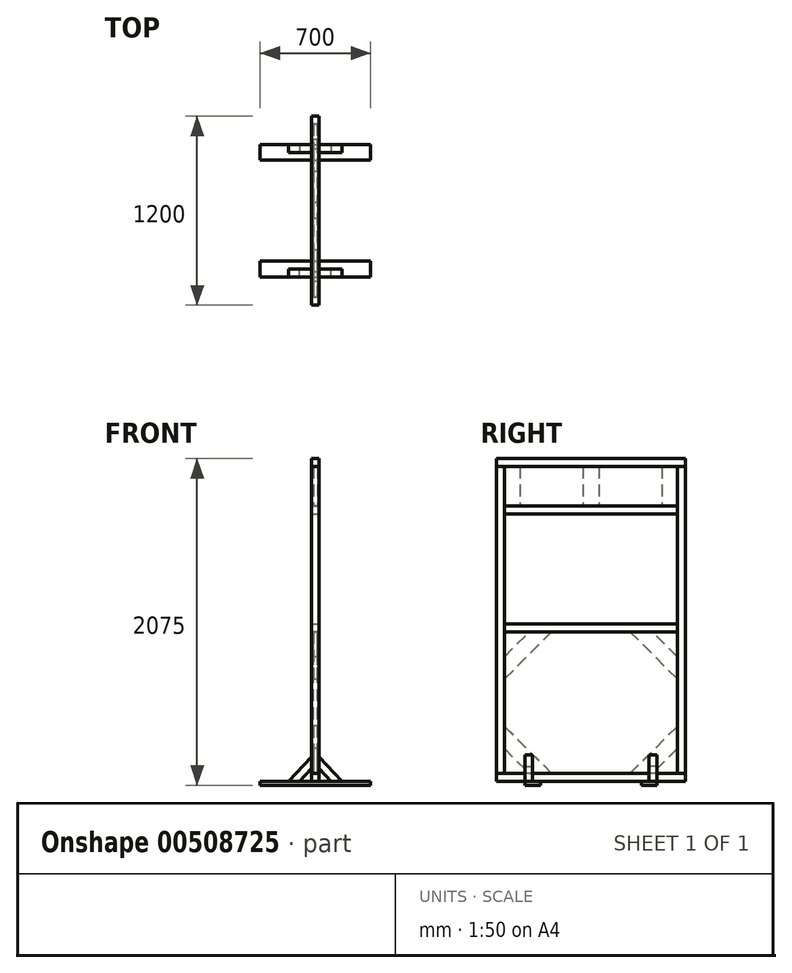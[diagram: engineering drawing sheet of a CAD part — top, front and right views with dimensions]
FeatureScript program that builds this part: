
annotation { "Feature Type Name" : "Feature", "Feature Type Description" : "" }
export const myFeature = defineFeature(function(context is Context, id is Id, definition is map)
    precondition{}
    {
        {
            var Q0;
            Q0=qCreatedBy(makeId("Top.planeOp"),FACE);
            var sketch = newSketch(context, id + "F0", { "sketchPlane" : qUnion([Q0])});
            skLineSegment(sketch, "E0.bottom", {"start": v(-350, 420) * mm, "end": v(350, 420) * mm});
            skLineSegment(sketch, "E0.top", {"start": v(-350, 320) * mm, "end": v(350, 320) * mm});
            skLineSegment(sketch, "E0.left", {"start": v(-350, 420) * mm, "end": v(-350, 320) * mm});
            skLineSegment(sketch, "E0.right", {"start": v(350, 420) * mm, "end": v(350, 320) * mm});
            skLineSegment(sketch, "E1.bottom", {"start": v(-350, -320) * mm, "end": v(350, -320) * mm});
            skLineSegment(sketch, "E1.top", {"start": v(-350, -420) * mm, "end": v(350, -420) * mm});
            skLineSegment(sketch, "E1.left", {"start": v(-350, -320) * mm, "end": v(-350, -420) * mm});
            skLineSegment(sketch, "E1.right", {"start": v(350, -320) * mm, "end": v(350, -420) * mm});
            skSolve(sketch);
        }
        {
            var Q0;
            Q0=makeQuery(id+"F0.imprint","IMPRINT",FACE,{"disambiguationData":[TD([[makeQuery(id+"F0.imprint","IMPRINT",EDGE,{"derivedFrom":sQuery(id+"F0.wireOp",EDGE,"E0.bottom")}),-1.0]])]});
            var Q1;
            Q1=makeQuery(id+"F0.imprint","IMPRINT",FACE,{"disambiguationData":[TD([[makeQuery(id+"F0.imprint","IMPRINT",EDGE,{"derivedFrom":sQuery(id+"F0.wireOp",EDGE,"E1.bottom")}),-1.0]])]});
            extrude(context, id + "F1", {"entities" : qUnion([Q0, Q1]), "depth" : 25 * mm});
        }
        {
            var Q0;
            Q0=makeQuery(id+"F1.opExtrude","CAP_FACE",FACE,{"disambiguationData":[OSD([sQuery(id+"F0.wireOp",EDGE,"E0.bottom"),sQuery(id+"F0.wireOp",EDGE,"E0.top"),sQuery(id+"F0.wireOp",EDGE,"E0.left"),sQuery(id+"F0.wireOp",EDGE,"E0.right")])],"isStart":false});
            var sketch = newSketch(context, id + "F2", { "sketchPlane" : qUnion([Q0])});
            skSolve(sketch);
        }
        {
            var Q0;
            Q0=makeQuery(id+"F1.opExtrude","CAP_FACE",FACE,{"disambiguationData":[OSD([sQuery(id+"F0.wireOp",EDGE,"E1.bottom"),sQuery(id+"F0.wireOp",EDGE,"E1.top"),sQuery(id+"F0.wireOp",EDGE,"E1.left"),sQuery(id+"F0.wireOp",EDGE,"E1.right")])],"isStart":false});
            var sketch = newSketch(context, id + "F3", { "sketchPlane" : qUnion([Q0])});
            skLineSegment(sketch, "E2.bottom", {"start": v(-25, 600) * mm, "end": v(25, 600) * mm});
            skLineSegment(sketch, "E2.top", {"start": v(-25, -600) * mm, "end": v(25, -600) * mm});
            skLineSegment(sketch, "E2.left", {"start": v(-25, 600) * mm, "end": v(-25, -600) * mm});
            skLineSegment(sketch, "E2.right", {"start": v(25, 600) * mm, "end": v(25, -600) * mm});
            skPoint(sketch, "E2.middle", {"position": v(0, 0) * mm});
            skSolve(sketch);
        }
        {
            var Q0;
            {var subQ0=sQuery(id+"F3.wireOp",EDGE,"E2.top");Q0=makeQuery(id+"F3.imprint","IMPRINT",FACE,{"disambiguationData":[TD([[makeQuery(id+"F3.imprint","IMPRINT",EDGE,{"derivedFrom":subQ0}),1.0]])]});}
            var Q1;
            {var subQ0=sQuery(id+"F3.wireOp",EDGE,"E2.left");var subQ1=makeQuery(id+"F1.opExtrude","CAP_EDGE",EDGE,{"disambiguationData":[OSD([sQuery(id+"F0.wireOp",EDGE,"E1.bottom")])],"isStart":false});var subQ2=makeQuery(id+"F3.imprint","INTERSECT",VERTEX,{"derivedFrom":[subQ1,subQ0]});Q1=makeQuery(id+"F3.imprint","IMPRINT",FACE,{"disambiguationData":[TD([[makeQuery(id+"F3.imprint","IMPRINT",EDGE,{"disambiguationData":[TD([[subQ2,-1.0]])],"derivedFrom":subQ0}),1.0]])]});}
            var Q2;
            {var subQ0=sQuery(id+"F3.wireOp",EDGE,"E2.bottom");Q2=makeQuery(id+"F3.imprint","IMPRINT",FACE,{"disambiguationData":[TD([[makeQuery(id+"F3.imprint","IMPRINT",EDGE,{"derivedFrom":subQ0}),-1.0]])]});}
            extrude(context, id + "F4", {"entities" : qUnion([Q0, Q1, Q2]), "depth" : 50 * mm});
        }
        {
            var Q0;
            Q0=makeQuery(id+"F2.imprint","IMPRINT",FACE,{"disambiguationData":[TD([[makeQuery(id+"F2.imprint","IMPRINT",EDGE,{"derivedFrom":makeQuery(id+"F1.opExtrude","CAP_EDGE",EDGE,{"disambiguationData":[OSD([sQuery(id+"F0.wireOp",EDGE,"E0.bottom")])],"isStart":false})}),-1.0]])]});
            var sketch = newSketch(context, id + "F5", { "sketchPlane" : qUnion([Q0])});
            skLineSegment(sketch, "E3.bottom", {"start": v(25, -600) * mm, "end": v(-25, -600) * mm});
            skLineSegment(sketch, "E3.top", {"start": v(25, 600) * mm, "end": v(-25, 600) * mm});
            skLineSegment(sketch, "E3.left", {"start": v(25, -600) * mm, "end": v(25, 600) * mm});
            skLineSegment(sketch, "E3.right", {"start": v(-25, -600) * mm, "end": v(-25, 600) * mm});
            skPoint(sketch, "E3.middle", {"position": v(0, 0) * mm});
            skSolve(sketch);
        }
        {
            var Q0;
            Q0=makeQuery(id+"F4.opExtrude","CAP_FACE",FACE,{"disambiguationData":[OSD([sQuery(id+"F3.wireOp",EDGE,"E2.bottom"),sQuery(id+"F3.wireOp",EDGE,"E2.top"),sQuery(id+"F3.wireOp",EDGE,"E2.left"),sQuery(id+"F3.wireOp",EDGE,"E2.right")])],"isStart":false});
            var sketch = newSketch(context, id + "F6", { "sketchPlane" : qUnion([Q0])});
            skSolve(sketch);
        }
        {
            var Q0;
            Q0=makeQuery(id+"F6.imprint","IMPRINT",FACE,{"disambiguationData":[TD([[makeQuery(id+"F6.imprint","IMPRINT",EDGE,{"derivedFrom":makeQuery(id+"F4.opExtrude","CAP_EDGE",EDGE,{"disambiguationData":[OSD([sQuery(id+"F3.wireOp",EDGE,"E2.bottom")])],"isStart":false})}),-1.0]])]});
            var sketch = newSketch(context, id + "F7", { "sketchPlane" : qUnion([Q0])});
            skLineSegment(sketch, "E4.bottom", {"start": v(25, -600) * mm, "end": v(-25, -600) * mm});
            skLineSegment(sketch, "E4.top", {"start": v(25, -550) * mm, "end": v(-25, -550) * mm});
            skLineSegment(sketch, "E4.left", {"start": v(25, -600) * mm, "end": v(25, -550) * mm});
            skLineSegment(sketch, "E4.right", {"start": v(-25, -600) * mm, "end": v(-25, -550) * mm});
            skPoint(sketch, "E4.middle", {"position": v(0, -575) * mm});
            skLineSegment(sketch, "E5.MirrorCS", {"start": v(25, 550) * mm, "end": v(-25, 550) * mm});
            skLineSegment(sketch, "E6.MirrorCS", {"start": v(25, 600) * mm, "end": v(25, 550) * mm});
            skLineSegment(sketch, "E7.MirrorCS", {"start": v(25, 600) * mm, "end": v(-25, 600) * mm});
            skLineSegment(sketch, "E8.MirrorCS", {"start": v(-25, 600) * mm, "end": v(-25, 550) * mm});
            skSolve(sketch);
        }
        {
            var Q0;
            Q0 = qSketchRegion(id + "F7", true);
            extrude(context, id + "F8", {"entities" : qUnion([Q0]), "depth" : 1950 * mm});
        }
        {
            var Q0;
            Q0=makeQuery(id+"F8.opExtrude","CAP_FACE",FACE,{"disambiguationData":[OSD([sQuery(id+"F7.wireOp",EDGE,"E4.bottom"),sQuery(id+"F7.wireOp",EDGE,"E4.top"),sQuery(id+"F7.wireOp",EDGE,"E4.left"),sQuery(id+"F7.wireOp",EDGE,"E4.right")])],"isStart":false});
            var sketch = newSketch(context, id + "F9", { "sketchPlane" : qUnion([Q0])});
            skLineSegment(sketch, "E9.bottom", {"start": v(25, -600) * mm, "end": v(-25, -600) * mm});
            skLineSegment(sketch, "E9.top", {"start": v(25, 600) * mm, "end": v(-25, 600) * mm});
            skLineSegment(sketch, "E9.left", {"start": v(25, -600) * mm, "end": v(25, 600) * mm});
            skLineSegment(sketch, "E9.right", {"start": v(-25, -600) * mm, "end": v(-25, 600) * mm});
            skPoint(sketch, "E9.middle", {"position": v(0, 0) * mm});
            skSolve(sketch);
        }
        {
            var Q0;
            {var subQ0=sQuery(id+"F9.wireOp",EDGE,"E9.top");Q0=makeQuery(id+"F9.imprint","IMPRINT",FACE,{"disambiguationData":[TD([[makeQuery(id+"F9.imprint","IMPRINT",EDGE,{"derivedFrom":subQ0}),1.0]])]});}
            var Q1;
            {var subQ0=sQuery(id+"F9.wireOp",EDGE,"E9.bottom");Q1=makeQuery(id+"F9.imprint","IMPRINT",FACE,{"disambiguationData":[TD([[makeQuery(id+"F9.imprint","IMPRINT",EDGE,{"derivedFrom":subQ0}),1.0]])]});}
            extrude(context, id + "F10", {"entities" : qUnion([Q0, Q1]), "depth" : 50 * mm});
        }
        {
            var Q0;
            Q0=makeQuery(id+"F8.opExtrude","SWEPT_FACE",FACE,{"disambiguationData":[OSD([sQuery(id+"F7.wireOp",EDGE,"E5.MirrorCS")])]});
            var sketch = newSketch(context, id + "F11", { "sketchPlane" : qUnion([Q0])});
            skLineSegment(sketch, "E10.bottom", {"start": v(-25, 1025) * mm, "end": v(25, 1025) * mm});
            skLineSegment(sketch, "E10.top", {"start": v(-25, 975) * mm, "end": v(25, 975) * mm});
            skLineSegment(sketch, "E10.left", {"start": v(-25, 1025) * mm, "end": v(-25, 975) * mm});
            skLineSegment(sketch, "E10.right", {"start": v(25, 1025) * mm, "end": v(25, 975) * mm});
            skLineSegment(sketch, "E11.bottom", {"start": v(-25, 1775) * mm, "end": v(25, 1775) * mm});
            skLineSegment(sketch, "E11.top", {"start": v(-25, 1725) * mm, "end": v(25, 1725) * mm});
            skLineSegment(sketch, "E11.left", {"start": v(-25, 1775) * mm, "end": v(-25, 1725) * mm});
            skLineSegment(sketch, "E11.right", {"start": v(25, 1775) * mm, "end": v(25, 1725) * mm});
            skSolve(sketch);
        }
        {
            var Q0;
            Q0 = qSketchRegion(id + "F11", true);
            extrude(context, id + "F12", {"entities" : qUnion([Q0]), "depth" : 1100 * mm});
        }
        {
            var Q0;
            Q0=qCreatedBy(makeId("Right.planeOp"),FACE);
            var sketch = newSketch(context, id + "F13", { "sketchPlane" : qUnion([Q0])});
            skLineSegment(sketch, "E12", {"start": v(-390.66, 975) * mm, "end": v(-249.3, 975) * mm});
            skLineSegment(sketch, "E13", {"start": v(-249.3, 975) * mm, "end": v(-550, 674.08) * mm});
            skLineSegment(sketch, "E14", {"start": v(-550, 674.08) * mm, "end": v(-550, 815.55) * mm});
            skLineSegment(sketch, "E15", {"start": v(-550, 815.55) * mm, "end": v(-390.66, 975) * mm});
            skLineSegment(sketch, "E16.MirrorCS", {"start": v(249.3, 975) * mm, "end": v(550, 674.08) * mm});
            skLineSegment(sketch, "E17.MirrorCS", {"start": v(550, 815.55) * mm, "end": v(390.66, 975) * mm});
            skLineSegment(sketch, "E18.MirrorCS", {"start": v(390.66, 975) * mm, "end": v(249.3, 975) * mm});
            skLineSegment(sketch, "E19.MirrorCS", {"start": v(550, 674.08) * mm, "end": v(550, 815.55) * mm});
            skLineSegment(sketch, "E20", {"start": v(-550, 525) * mm, "end": v(550, 525) * mm, "construction": true});
            skLineSegment(sketch, "E21.MirrorCS", {"start": v(-249.3, 75) * mm, "end": v(-550, 375.92) * mm});
            skLineSegment(sketch, "E22.MirrorCS", {"start": v(-550, 375.92) * mm, "end": v(-550, 234.45) * mm});
            skLineSegment(sketch, "E23.MirrorCS", {"start": v(-550, 234.45) * mm, "end": v(-390.66, 75) * mm});
            skLineSegment(sketch, "E24.MirrorCS", {"start": v(-390.66, 75) * mm, "end": v(-249.3, 75) * mm});
            skLineSegment(sketch, "E25.MirrorCS", {"start": v(249.3, 75) * mm, "end": v(550, 375.92) * mm});
            skLineSegment(sketch, "E26.MirrorCS", {"start": v(550, 234.45) * mm, "end": v(390.66, 75) * mm});
            skLineSegment(sketch, "E27.MirrorCS", {"start": v(390.66, 75) * mm, "end": v(249.3, 75) * mm});
            skLineSegment(sketch, "E28.MirrorCS", {"start": v(550, 375.92) * mm, "end": v(550, 234.45) * mm});
            skLineSegment(sketch, "E29.bottom", {"start": v(550, 2025) * mm, "end": v(450, 2025) * mm});
            skLineSegment(sketch, "E29.top", {"start": v(550, 1775) * mm, "end": v(450, 1775) * mm});
            skLineSegment(sketch, "E29.left", {"start": v(550, 2025) * mm, "end": v(550, 1775) * mm});
            skLineSegment(sketch, "E29.right", {"start": v(450, 2025) * mm, "end": v(450, 1775) * mm});
            skLineSegment(sketch, "E30.bottom", {"start": v(-450, 2025) * mm, "end": v(-550, 2025) * mm});
            skLineSegment(sketch, "E30.top", {"start": v(-450, 1775) * mm, "end": v(-550, 1775) * mm});
            skLineSegment(sketch, "E30.left", {"start": v(-450, 2025) * mm, "end": v(-450, 1775) * mm});
            skLineSegment(sketch, "E30.right", {"start": v(-550, 2025) * mm, "end": v(-550, 1775) * mm});
            skLineSegment(sketch, "E31.bottom", {"start": v(50, 2025) * mm, "end": v(-50, 2025) * mm});
            skLineSegment(sketch, "E31.top", {"start": v(50, 1775) * mm, "end": v(-50, 1775) * mm});
            skLineSegment(sketch, "E31.left", {"start": v(50, 2025) * mm, "end": v(50, 1775) * mm});
            skLineSegment(sketch, "E31.right", {"start": v(-50, 2025) * mm, "end": v(-50, 1775) * mm});
            skSolve(sketch);
        }
        {
            var Q0;
            Q0 = qSketchRegion(id + "F13", true);
            extrude(context, id + "F14", {"entities" : qUnion([Q0]), "depth" : 13 * mm, "hasSecondDirection" : true, "secondDirectionOppositeDirection" : true, "secondDirectionDepth" : 13 * mm});
        }
        {
            var Q0;
            Q0=qCreatedBy(makeId("Front.planeOp"),FACE);
            cPlane(context, id + "F15", {"entities" : qUnion([Q0]), "cplaneType" : CPlaneType.OFFSET, "offset" : 370 * mm, "oppositeDirection" : true, "width" : 150 * mm, "height" : 150 * mm});
        }
        {
            var Q0;
            Q0=qCreatedBy(id+"F15.planeOp",FACE);
            var sketch = newSketch(context, id + "F16", { "sketchPlane" : qUnion([Q0])});
            skLineSegment(sketch, "E32", {"start": v(100.72, 25) * mm, "end": v(13, 118.99) * mm});
            skLineSegment(sketch, "E33", {"start": v(13, 118.99) * mm, "end": v(13, 192.27) * mm});
            skLineSegment(sketch, "E34", {"start": v(13, 192.27) * mm, "end": v(169.11, 25) * mm});
            skLineSegment(sketch, "E35", {"start": v(169.11, 25) * mm, "end": v(100.72, 25) * mm});
            skSolve(sketch);
        }
        {
            var Q0;
            Q0 = qSketchRegion(id + "F16", true);
            extrude(context, id + "F17", {"entities" : qUnion([Q0]), "oppositeDirection" : true, "depth" : 50 * mm});
        }
        {
            var Q0;
            Q0=makeQuery(id+"F17.opExtrude","SWEPT_BODY",BODY,{"disambiguationData":[OSD([sQuery(id+"F16.wireOp",EDGE,"E32"),sQuery(id+"F16.wireOp",EDGE,"E33"),sQuery(id+"F16.wireOp",EDGE,"E34"),sQuery(id+"F16.wireOp",EDGE,"E35")])]});
            var Q1;
            Q1=qCreatedBy(makeId("Front.planeOp"),FACE);
            mirror(context, id + "F18", {"entities" : qUnion([Q0]), "mirrorPlane" : qUnion([Q1])});
        }
        {
            var Q0;
            Q0=makeQuery(id+"F18.opPattern","COPY",BODY,{"derivedFrom":makeQuery(id+"F17.opExtrude","SWEPT_BODY",BODY,{"disambiguationData":[OSD([sQuery(id+"F16.wireOp",EDGE,"E32"),sQuery(id+"F16.wireOp",EDGE,"E33"),sQuery(id+"F16.wireOp",EDGE,"E34"),sQuery(id+"F16.wireOp",EDGE,"E35")])]}),"instanceName":"1"});
            var Q1;
            Q1=makeQuery(id+"F17.opExtrude","SWEPT_BODY",BODY,{"disambiguationData":[OSD([sQuery(id+"F16.wireOp",EDGE,"E32"),sQuery(id+"F16.wireOp",EDGE,"E33"),sQuery(id+"F16.wireOp",EDGE,"E34"),sQuery(id+"F16.wireOp",EDGE,"E35")])]});
            var Q2;
            Q2=qCreatedBy(makeId("Right.planeOp"),FACE);
            mirror(context, id + "F19", {"entities" : qUnion([Q0, Q1]), "mirrorPlane" : qUnion([Q2])});
        }
        {
            var Q0;
            Q0=makeQuery(id+"F14.opExtrude","CAP_FACE",FACE,{"disambiguationData":[OSD([sQuery(id+"F13.wireOp",EDGE,"E16.MirrorCS"),sQuery(id+"F13.wireOp",EDGE,"E17.MirrorCS"),sQuery(id+"F13.wireOp",EDGE,"E18.MirrorCS"),sQuery(id+"F13.wireOp",EDGE,"E19.MirrorCS")])],"isStart":true});
            var sketch = newSketch(context, id + "F20", { "sketchPlane" : qUnion([Q0])});
            skLineSegment(sketch, "E36.0", {"start": v(550, 975) * mm, "end": v(-550, 975) * mm});
            skLineSegment(sketch, "E37", {"start": v(-550, 975) * mm, "end": v(-550, 75) * mm});
            skLineSegment(sketch, "E38", {"start": v(-550, 75) * mm, "end": v(-420, 75) * mm});
            skLineSegment(sketch, "E39", {"start": v(-420, 75) * mm, "end": v(-420, 192.27) * mm});
            skLineSegment(sketch, "E40", {"start": v(-420, 192.27) * mm, "end": v(-370, 192.27) * mm});
            skLineSegment(sketch, "E41", {"start": v(-370, 192.27) * mm, "end": v(-370, 75.15) * mm});
            skLineSegment(sketch, "E42", {"start": v(-370, 75.15) * mm, "end": v(370, 75.15) * mm});
            skLineSegment(sketch, "E43", {"start": v(370, 75.15) * mm, "end": v(370, 192.27) * mm});
            skLineSegment(sketch, "E44", {"start": v(370, 192.27) * mm, "end": v(420, 192.27) * mm});
            skLineSegment(sketch, "E45", {"start": v(420, 192.27) * mm, "end": v(420, 75) * mm});
            skLineSegment(sketch, "E46", {"start": v(420, 75) * mm, "end": v(550, 75) * mm});
            skLineSegment(sketch, "E47", {"start": v(550, 75) * mm, "end": v(550, 975) * mm});
            skLineSegment(sketch, "E48.bottom", {"start": v(-550, 2025) * mm, "end": v(550, 2025) * mm});
            skLineSegment(sketch, "E48.top", {"start": v(-550, 1775) * mm, "end": v(550, 1775) * mm});
            skLineSegment(sketch, "E48.left", {"start": v(-550, 2025) * mm, "end": v(-550, 1775) * mm});
            skLineSegment(sketch, "E48.right", {"start": v(550, 2025) * mm, "end": v(550, 1775) * mm});
            skSolve(sketch);
        }
        {
            var Q0;
            Q0 = qSketchRegion(id + "F20", true);
            extrude(context, id + "F21", {"entities" : qUnion([Q0]), "depth" : 9 * mm});
        }
        {
            var Q0;
            Q0=makeQuery(id+"F21.opExtrude","SWEPT_BODY",BODY,{"disambiguationData":[OSD([sQuery(id+"F20.wireOp",EDGE,"E36.0"),sQuery(id+"F20.wireOp",EDGE,"E37"),sQuery(id+"F20.wireOp",EDGE,"E38"),sQuery(id+"F20.wireOp",EDGE,"E39"),sQuery(id+"F20.wireOp",EDGE,"E40"),sQuery(id+"F20.wireOp",EDGE,"E41"),sQuery(id+"F20.wireOp",EDGE,"E42"),sQuery(id+"F20.wireOp",EDGE,"E43"),sQuery(id+"F20.wireOp",EDGE,"E44"),sQuery(id+"F20.wireOp",EDGE,"E45"),sQuery(id+"F20.wireOp",EDGE,"E46"),sQuery(id+"F20.wireOp",EDGE,"E47")])]});
            var Q1;
            Q1=makeQuery(id+"F21.opExtrude","SWEPT_BODY",BODY,{"disambiguationData":[OSD([sQuery(id+"F20.wireOp",EDGE,"E48.bottom"),sQuery(id+"F20.wireOp",EDGE,"E48.top"),sQuery(id+"F20.wireOp",EDGE,"E48.left"),sQuery(id+"F20.wireOp",EDGE,"E48.right")])]});
            var Q2;
            Q2=qCreatedBy(makeId("Right.planeOp"),FACE);
            mirror(context, id + "F22", {"entities" : qUnion([Q0, Q1]), "mirrorPlane" : qUnion([Q2])});
        }
    });
